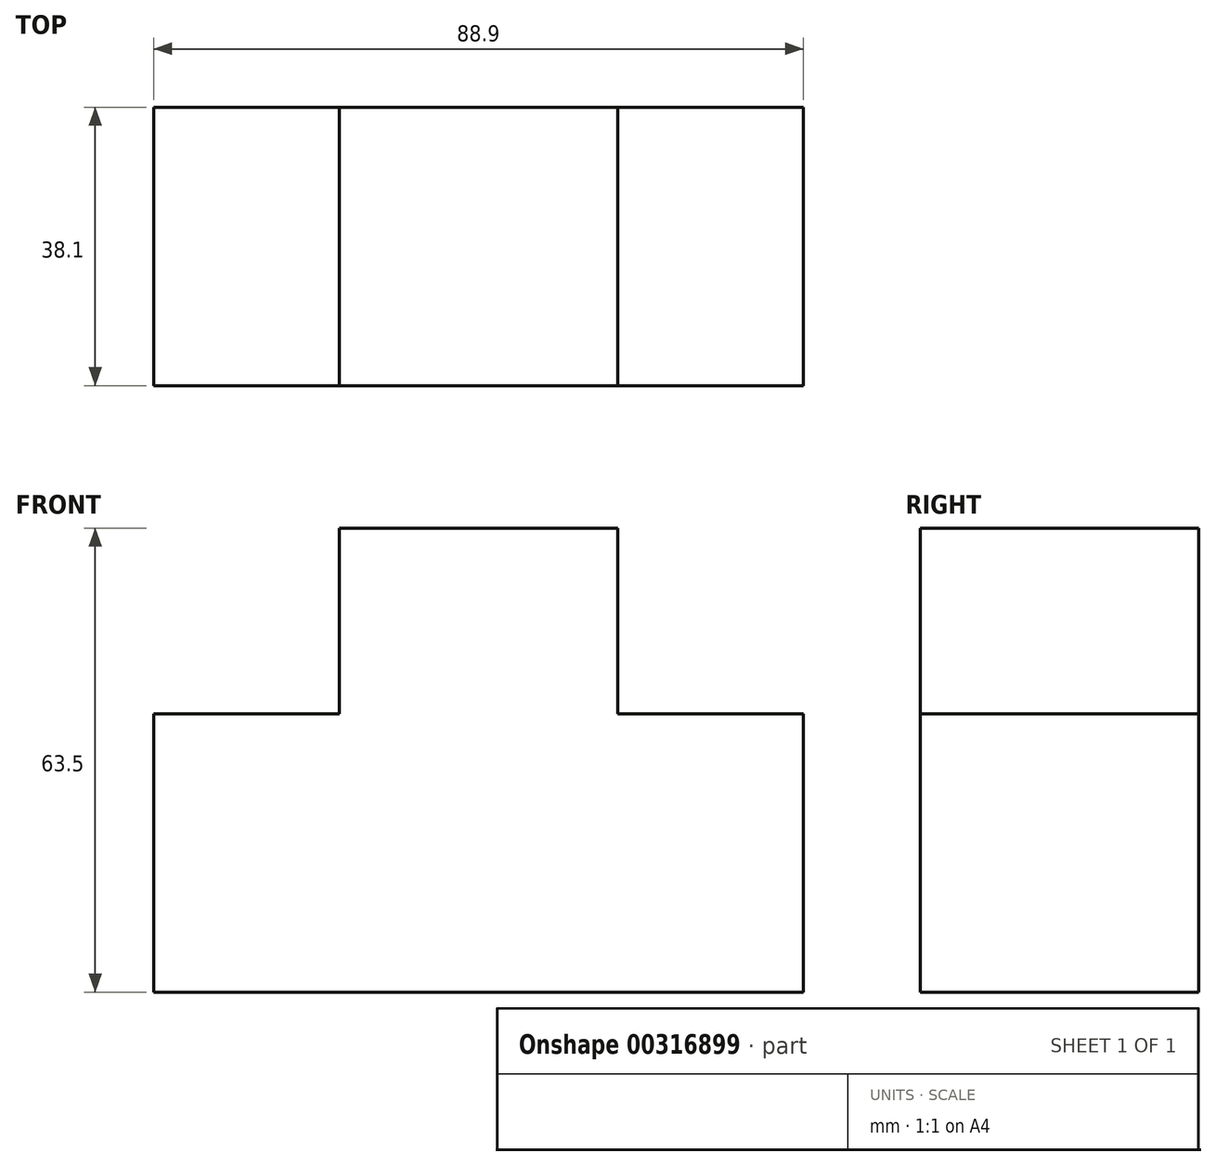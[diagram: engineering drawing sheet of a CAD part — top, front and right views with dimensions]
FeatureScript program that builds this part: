
annotation { "Feature Type Name" : "Feature", "Feature Type Description" : "" }
export const myFeature = defineFeature(function(context is Context, id is Id, definition is map)
    precondition{}
    {
        {
            var Q0;
            Q0=qCreatedBy(makeId("Front.planeOp"),FACE);
            var sketch = newSketch(context, id + "F0", { "sketchPlane" : qUnion([Q0])});
            skLineSegment(sketch, "E0", {"start": v(-87.26, -56.71) * mm, "end": v(-87.26, -18.61) * mm});
            skLineSegment(sketch, "E1", {"start": v(-87.26, -18.61) * mm, "end": v(-61.86, -18.61) * mm});
            skLineSegment(sketch, "E2", {"start": v(-61.86, -18.61) * mm, "end": v(-61.86, 6.79) * mm});
            skLineSegment(sketch, "E3", {"start": v(-61.86, 6.79) * mm, "end": v(-23.76, 6.79) * mm});
            skLineSegment(sketch, "E4", {"start": v(-23.76, 6.79) * mm, "end": v(-23.76, -18.61) * mm});
            skLineSegment(sketch, "E5", {"start": v(-23.76, -18.61) * mm, "end": v(1.64, -18.61) * mm});
            skLineSegment(sketch, "E6", {"start": v(1.64, -18.61) * mm, "end": v(1.64, -56.71) * mm});
            skLineSegment(sketch, "E7", {"start": v(-87.26, -56.71) * mm, "end": v(1.64, -56.71) * mm});
            skSolve(sketch);
        }
        {
            var Q0;
            Q0=makeQuery(id+"F0.imprint","IMPRINT",FACE,{"disambiguationData":[TD([[makeQuery(id+"F0.imprint","IMPRINT",EDGE,{"derivedFrom":sQuery(id+"F0.wireOp",EDGE,"E0")}),-1.0]])]});
            extrude(context, id + "F1", {"entities" : qUnion([Q0]), "depth" : 38.1 * mm});
        }
    });
